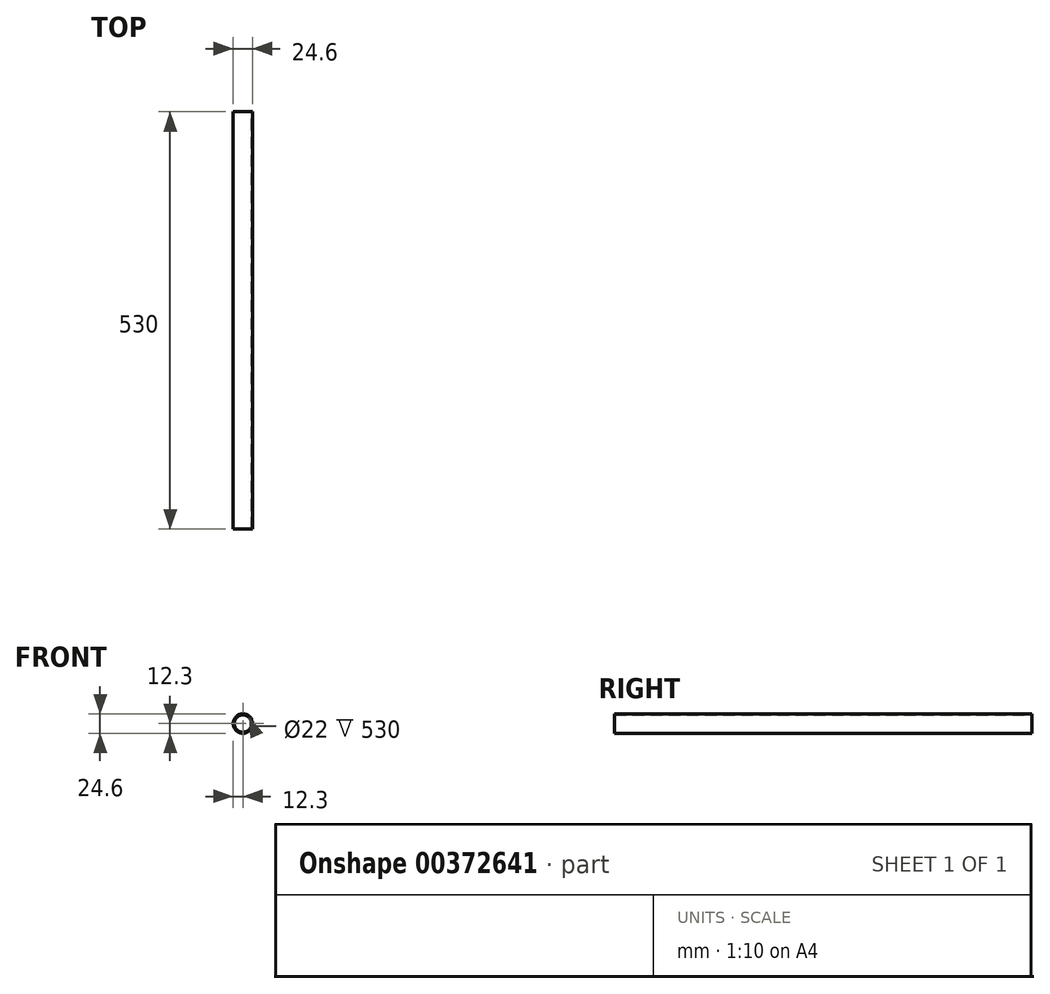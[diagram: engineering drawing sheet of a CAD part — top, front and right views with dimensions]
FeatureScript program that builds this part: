
annotation { "Feature Type Name" : "Feature", "Feature Type Description" : "" }
export const myFeature = defineFeature(function(context is Context, id is Id, definition is map)
    precondition{}
    {
        {
            var Q0;
            Q0=qCreatedBy(makeId("Front.planeOp"),FACE);
            var sketch = newSketch(context, id + "F0", { "sketchPlane" : qUnion([Q0])});
            skCircle(sketch, "E0", {"center": v(0, 0) * mm, "radius": 12.3 * mm});
            skCircle(sketch, "E1", {"center": v(0, 0) * mm, "radius": 11 * mm});
            skSolve(sketch);
        }
        {
            var Q0;
            Q0 = qSketchRegion(id + "F0", true);
            extrude(context, id + "F1", {"entities" : qUnion([Q0]), "depth" : 530 * mm, "offsetDistance" : 25 * mm});
        }
    });
